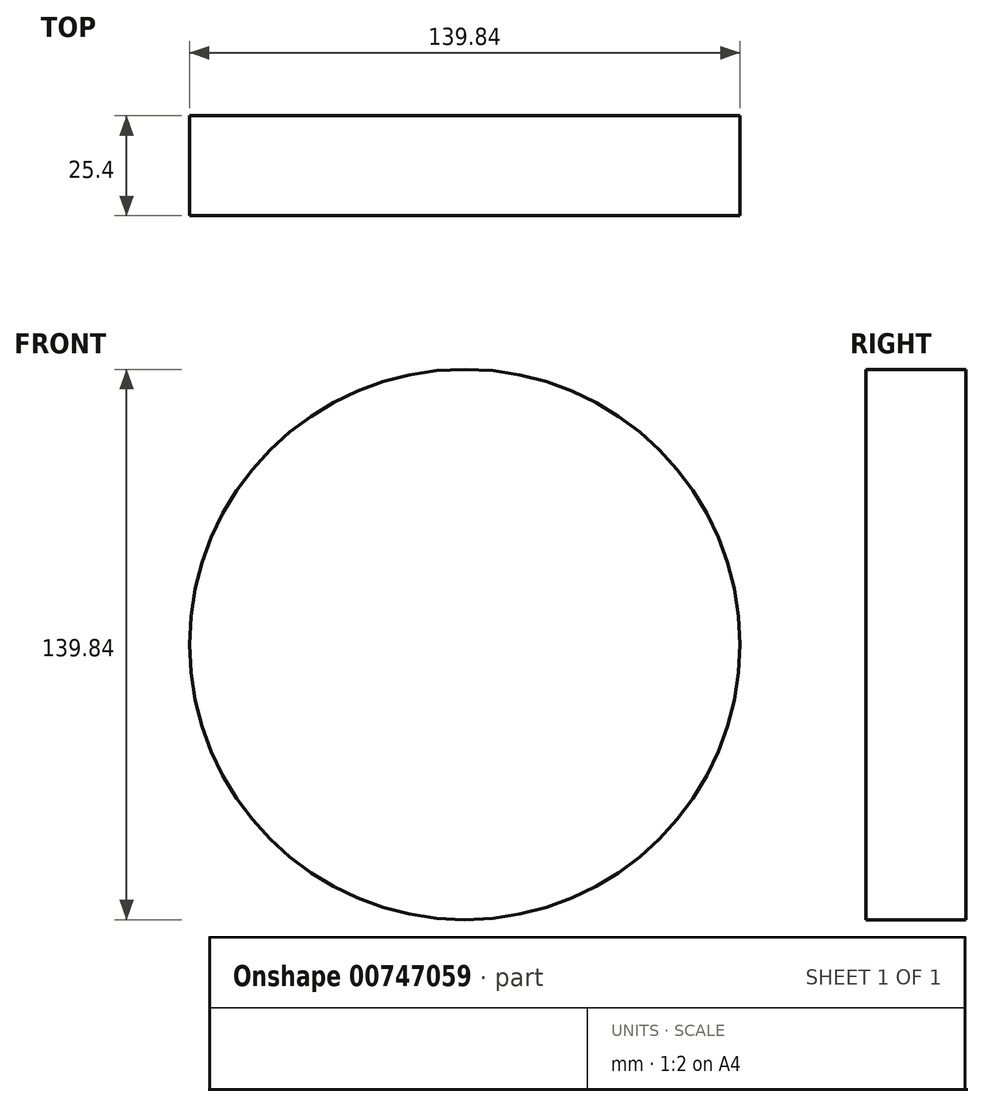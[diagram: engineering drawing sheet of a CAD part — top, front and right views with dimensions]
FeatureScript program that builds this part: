
annotation { "Feature Type Name" : "Feature", "Feature Type Description" : "" }
export const myFeature = defineFeature(function(context is Context, id is Id, definition is map)
    precondition{}
    {
        {
            var Q0;
            Q0=qCreatedBy(makeId("Front.planeOp"),FACE);
            var sketch = newSketch(context, id + "F0", { "sketchPlane" : qUnion([Q0])});
            skCircle(sketch, "E0", {"center": v(0, 0) * mm, "radius": 69.92 * mm});
            skSolve(sketch);
        }
        {
            var Q0;
            Q0=makeQuery(id+"F0.imprint","IMPRINT",FACE,{"disambiguationData":[TD([[makeQuery(id+"F0.imprint","IMPRINT",EDGE,{"derivedFrom":sQuery(id+"F0.wireOp",EDGE,"E0")}),1.0]])]});
            extrude(context, id + "F1", {"entities" : qUnion([Q0]), "depth" : 25.4 * mm, "offsetDistance" : 25.4 * mm});
        }
    });
